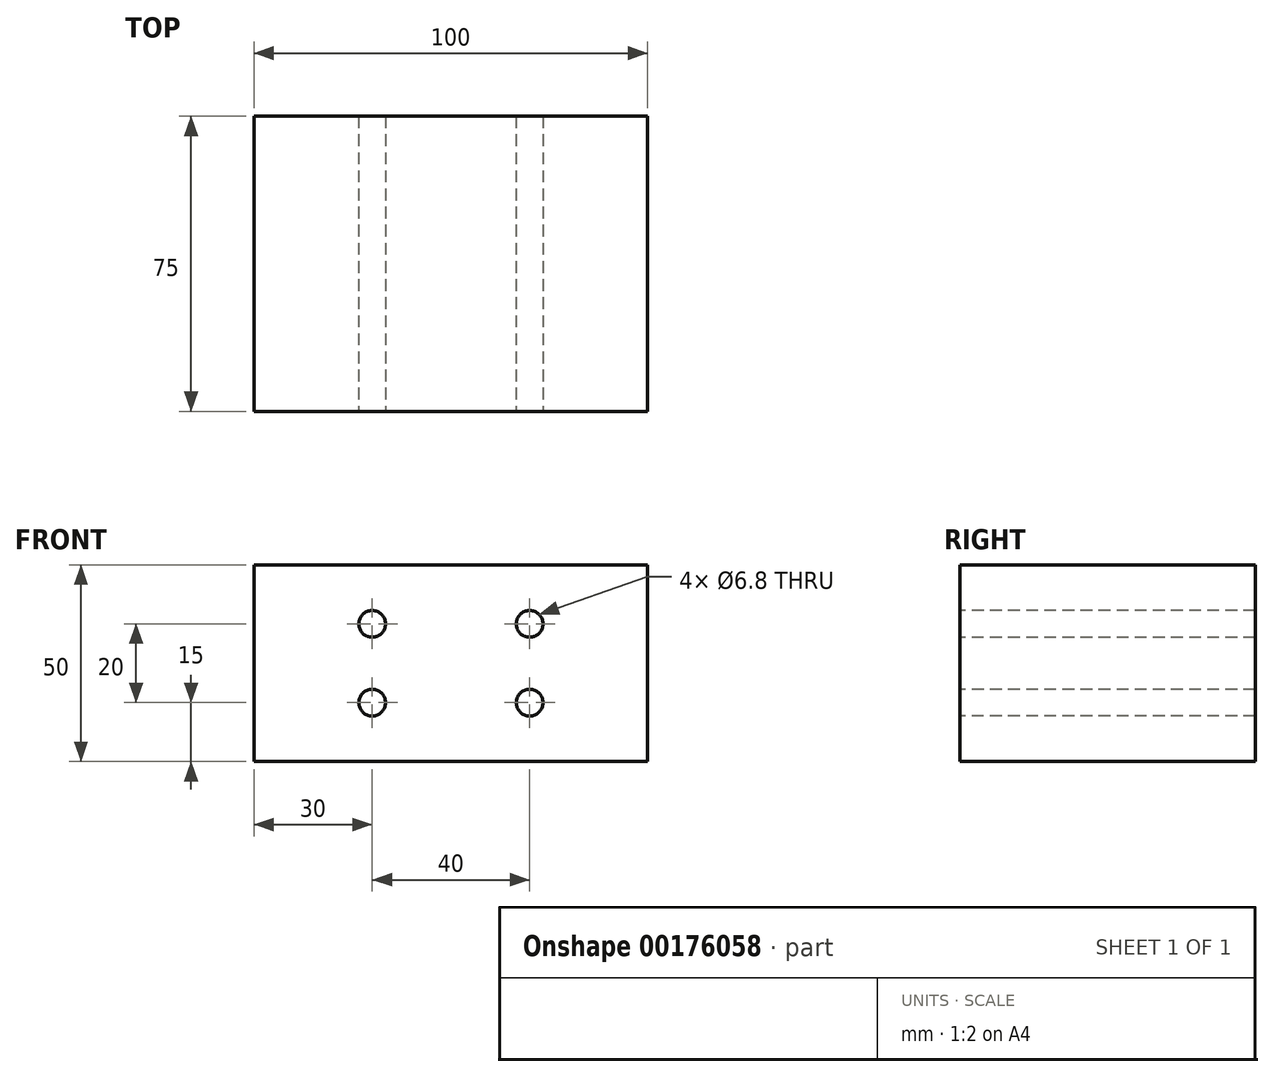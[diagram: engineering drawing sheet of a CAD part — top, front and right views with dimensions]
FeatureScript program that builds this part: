
annotation { "Feature Type Name" : "Feature", "Feature Type Description" : "" }
export const myFeature = defineFeature(function(context is Context, id is Id, definition is map)
    precondition{}
    {
        {
            var Q0;
            Q0=qCreatedBy(makeId("Front.planeOp"),FACE);
            var sketch = newSketch(context, id + "F0", { "sketchPlane" : qUnion([Q0])});
            skLineSegment(sketch, "E0.bottom", {"start": v(-50, 25) * mm, "end": v(50, 25) * mm});
            skLineSegment(sketch, "E0.top", {"start": v(-50, -25) * mm, "end": v(50, -25) * mm});
            skLineSegment(sketch, "E0.left", {"start": v(-50, 25) * mm, "end": v(-50, -25) * mm});
            skLineSegment(sketch, "E0.right", {"start": v(50, 25) * mm, "end": v(50, -25) * mm});
            skPoint(sketch, "E0.middle", {"position": v(0, 0) * mm});
            skSolve(sketch);
        }
        {
            var Q0;
            Q0=makeQuery(id+"F0.imprint","IMPRINT",FACE,{"disambiguationData":[TD([[makeQuery(id+"F0.imprint","IMPRINT",EDGE,{"derivedFrom":sQuery(id+"F0.wireOp",EDGE,"E0.bottom")}),-1.0]])]});
            extrude(context, id + "F1", {"entities" : qUnion([Q0]), "endBound" : BoundingType.SYMMETRIC, "depth" : 75 * mm});
        }
        {
            var Q0;
            Q0=makeQuery(id+"F1.opExtrude","CAP_FACE",FACE,{"disambiguationData":[OSD([sQuery(id+"F0.wireOp",EDGE,"E0.bottom"),sQuery(id+"F0.wireOp",EDGE,"E0.top"),sQuery(id+"F0.wireOp",EDGE,"E0.left"),sQuery(id+"F0.wireOp",EDGE,"E0.right")])],"isStart":false});
            var sketch = newSketch(context, id + "F2", { "sketchPlane" : qUnion([Q0])});
            skLineSegment(sketch, "E1", {"start": v(-50, 10) * mm, "end": v(-20, 10) * mm, "construction": true});
            skLineSegment(sketch, "E2", {"start": v(-20, 10) * mm, "end": v(-20, 25) * mm, "construction": true});
            skLineSegment(sketch, "E3.MirrorCS", {"start": v(20, 10) * mm, "end": v(20, 25) * mm, "construction": true});
            skLineSegment(sketch, "E4.MirrorCS", {"start": v(50, 10) * mm, "end": v(20, 10) * mm, "construction": true});
            skLineSegment(sketch, "E5.MirrorCS", {"start": v(50, -10) * mm, "end": v(20, -10) * mm, "construction": true});
            skLineSegment(sketch, "E6.MirrorCS", {"start": v(20, -10) * mm, "end": v(20, -25) * mm, "construction": true});
            skLineSegment(sketch, "E7.MirrorCS", {"start": v(-20, -10) * mm, "end": v(-20, -25) * mm, "construction": true});
            skLineSegment(sketch, "E8.MirrorCS", {"start": v(-50, -10) * mm, "end": v(-20, -10) * mm, "construction": true});
            skSolve(sketch);
        }
        {
            var Q0;
            Q0=sQuery(id+"F2.wireOp",VERTEX,"E2.start");
            var Q1;
            Q1=sQuery(id+"F2.wireOp",VERTEX,"E3.MirrorCS.start");
            var Q2;
            Q2=sQuery(id+"F2.wireOp",VERTEX,"E6.MirrorCS.start");
            var Q3;
            Q3=sQuery(id+"F2.wireOp",VERTEX,"E7.MirrorCS.start");
            var Q4;
            Q4=makeQuery(id+"F1.opExtrude","SWEPT_BODY",BODY,{"disambiguationData":[OSD([sQuery(id+"F0.wireOp",EDGE,"E0.bottom"),sQuery(id+"F0.wireOp",EDGE,"E0.top"),sQuery(id+"F0.wireOp",EDGE,"E0.left"),sQuery(id+"F0.wireOp",EDGE,"E0.right")])]});
            hole(context, id + "F3", {"style" : HoleStyle.SIMPLE, "endStyle" : HoleEndStyle.THROUGH, "standardTappedOrClearance" : lookupTablePath({ "standard" : "ISO", "engagement" : "75%", "pitch" : "1.25 mm", "size" : "M8", "type" : "Tapped" }), "standardBlindInLast" : lookupTablePath({ "standard" : "ISO", "engagement" : "75%", "pitch" : "1.25 mm", "size" : "M8", "type" : "Tapped" }), "holeDiameter" : 6.8 * mm, "startFromSketch" : true, "locations" : qUnion([Q0, Q1, Q2, Q3]), "scope" : qUnion([Q4]), "isTappedThrough" : true, "majorDiameter" : 8 * mm, "showTappedDepth" : true});
        }
    });
